# Revit family: Trennsteg -TSG 60 FS,DD,A2,A4,FT SO
name_source: partatom
category: Generic Models
revit_build: Autodesk Revit 2017 (Build: 20190508_0315(x64)
units: mm (PartAtom-declared; Revit-internal decimal feet)

## family parameters
Always vertical = Yes
Can host rebar = No
Cut with Voids When Loaded = No
Part Type = Normal
Room Calculation Point = No
Round Connector Dimension = Use Diameter
Shared = No
Work Plane-Based = No

## types (5) — shared parameters
Height = 56 mm  [stored 0.183727 ft]
Length = 3000 mm  [stored 9.84252 ft]
Manufacturer = OBO Bettermann
URL = http://www.obo-bettermann.com

## per-type parameters (varying)
| type | GTIN | Manufacturer Art.No. | Material |
| TSG 60 FS | 4012195694540 | 6062068 | Strip-galvanised |
| TSG 60 DD | 4012195694687 | 6062327 | Strip galvanised zinc/aluminium, Double Dip |
| TSG 60 FT SO | 4012195943686 | 7190495 | Hot-dip galvanised 85 µm |
| TSG 60 A2 | 4012195694557 | 6062084 | Stainless steel, A2 |
| TSG 60 A4 | 4012195694564 | 6062086 | Stainless steel, A4 |

note: column(s) folded — value = type name in every type: Article Type

note: [stored X ft] marks values corroborated as IEEE doubles in the binary element streams (Revit-internal decimal feet)

## geometry (parser evidence)
native form markers: Sweep x2
no freeform markers — native parametric forms only
